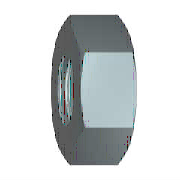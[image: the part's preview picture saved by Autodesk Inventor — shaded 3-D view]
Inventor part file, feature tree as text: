
AUTODESK INVENTOR PART (.ipt)
format: ipt  version: 2024 (Build 280153000, 153)  size: 161,792 bytes
history: native  units: mm (DEFAULTED — no unit token found)
features: chamfer x1, hole x1, other x1, plane x1
ambient origin geometry x7: Origin, YZ Plane, XZ Plane, X Axis, Y Axis, Z Axis, Center Point
bodies: Solid1 (feature_tree), Body (feature_tree)
feature tree (4):
  chamfer  "Chamfer1"  Distance=8.082904mm
  hole  "Thread"  [1 undecoded]
  other  "Work Axis1"
  plane  "Work Plane1"
note: 1 required parameter value undecoded (feature->parameter linkage not recoverable at this tier; creation-order binding heuristic only, values carry confidence <= 0.55)
